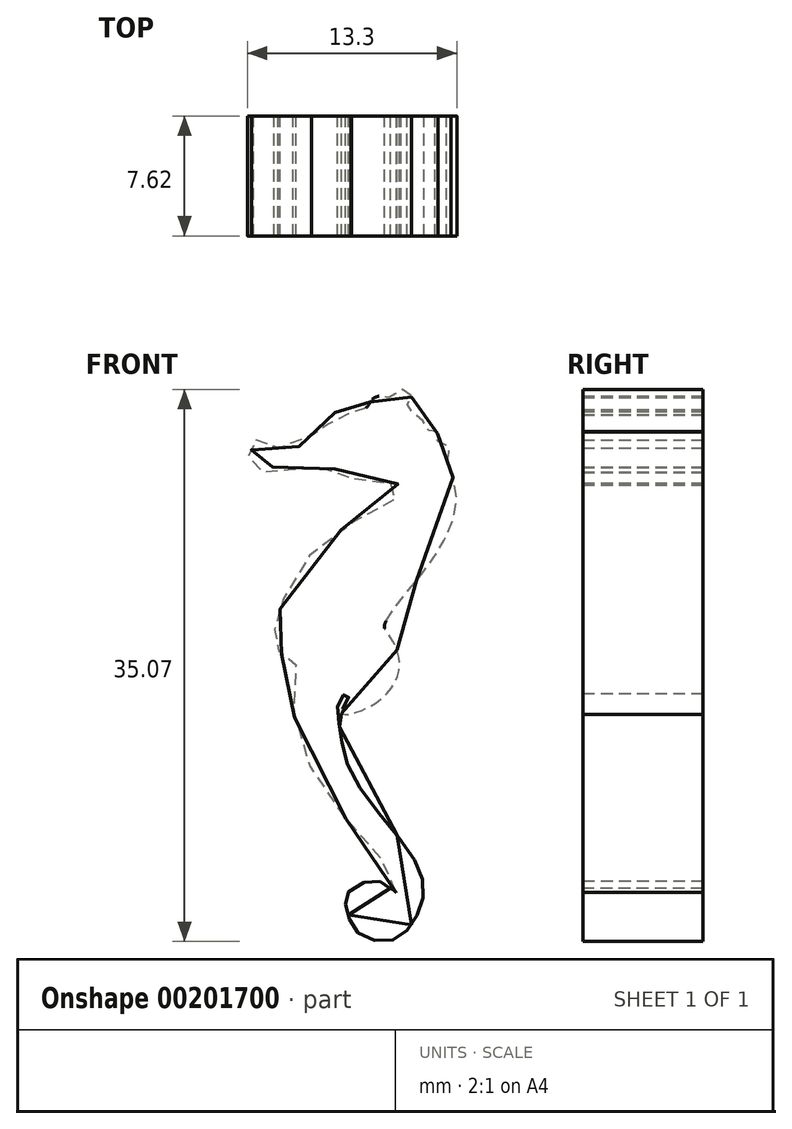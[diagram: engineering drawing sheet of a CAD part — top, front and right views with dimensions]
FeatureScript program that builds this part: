
annotation { "Feature Type Name" : "Feature", "Feature Type Description" : "" }
export const myFeature = defineFeature(function(context is Context, id is Id, definition is map)
    precondition{}
    {
        {
            var Q0;
            Q0=qCreatedBy(makeId("Front.planeOp"),FACE);
            var sketch = newSketch(context, id + "F0", { "sketchPlane" : qUnion([Q0])});
            skPoint(sketch, "E0.47.internal.snap0", {"position": v(0.25, -38.1) * mm});
            skPoint(sketch, "E0.74.internal.snap0", {"position": v(0.25, -38.1) * mm});
            skPoint(sketch, "E0.75.internal.snap0", {"position": v(0.25, -38.1) * mm});
            skFitSpline(sketch, "E0", {"points": [v(-1.93, -4.58) * mm, v(-2.28, -4.55) * mm, v(-2.23, -5.13) * mm, v(-4.01, -5.6) * mm, v(-5.21, -5.48) * mm, v(-5.56, -5.13) * mm, v(-6.06, -5.25) * mm, v(-6.12, -5.8) * mm, v(-6.35, -6.07) * mm, v(-6, -6.45) * mm, v(-5.97, -6.89) * mm, v(-5.3, -7.12) * mm, v(-4.83, -6.86) * mm, v(-3.28, -7) * mm, v(-2.23, -7.15) * mm, v(-1.38, -6.86) * mm, v(-0.47, -7.12) * mm, v(0.4, -7.62) * mm, v(2.51, -7.94) * mm, v(3.13, -7.85) * mm, v(3.39, -8.44) * mm, v(2.22, -9.32) * mm, v(0, -10.57) * mm, v(-2.7, -12.77) * mm, v(-4.07, -15.2) * mm, v(-4.52, -16.64) * mm, v(-4.63, -17.15) * mm, v(-4.29, -17.45) * mm, v(-4.39, -18.03) * mm, v(-4.19, -18.7) * mm, v(-3.37, -18.98) * mm, v(-3.27, -19.38) * mm, v(-3.44, -21.41) * mm, v(-2.87, -24.76) * mm, v(-0.87, -28.2) * mm, v(1.46, -30.91) * mm, v(3.02, -33.1) * mm, v(3.08, -33.85) * mm, v(2.61, -33.5) * mm, v(1.7, -33.1) * mm, v(0, -33.91) * mm, v(0, -35.06) * mm, v(0.72, -36.45) * mm, v(2.77, -36.9) * mm, v(4.18, -35.73) * mm, v(4.86, -33.68) * mm, v(3.76, -31.02) * mm, v(0.25, -26.28) * mm, v(-0.5, -23.36) * mm, v(-0.53, -21.65) * mm, v(0, -21.23) * mm, v(0, -21.68) * mm, v(-0.38, -22.48) * mm, v(1.78, -21.84) * mm, v(3.3, -19.3) * mm, v(2.58, -17.4) * mm, v(2.35, -16.9) * mm, v(3.76, -14.81) * mm, v(5.8, -12.08) * mm, v(6.93, -8.31) * mm, v(6.32, -6.06) * mm, v(6.56, -5.7) * mm, v(5.88, -5.25) * mm, v(5.56, -5.05) * mm, v(5.76, -4.61) * mm, v(5.28, -4.57) * mm, v(4.71, -3.8) * mm, v(3.79, -2.96) * mm, v(4.07, -2.32) * mm, v(3.27, -1.92) * mm, v(2.86, -2.4) * mm, v(2.22, -2.32) * mm, v(1.54, -2.56) * mm, v(1.25, -3) * mm, v(0.25, -3.48) * mm, v(0.25, -3.28) * mm, v(0, -3.48) * mm, v(-0.56, -3.16) * mm, v(-1.16, -4.05) * mm, v(-1.93, -4.58) * mm]});
            skFitSpline(sketch, "E1", {"points": [v(3.08, -33.85) * mm, v(1.46, -33.85) * mm, v(1.46, -35.06) * mm, v(2.61, -35.73) * mm, v(3.08, -33.85) * mm]});
            skSolve(sketch);
        }
        {
            var Q0;
            Q0 = qSketchRegion(id + "F0", true);
            extrude(context, id + "F1", {"entities" : qUnion([Q0]), "oppositeDirection" : true, "depth" : 7.62 * mm});
        }
    });
